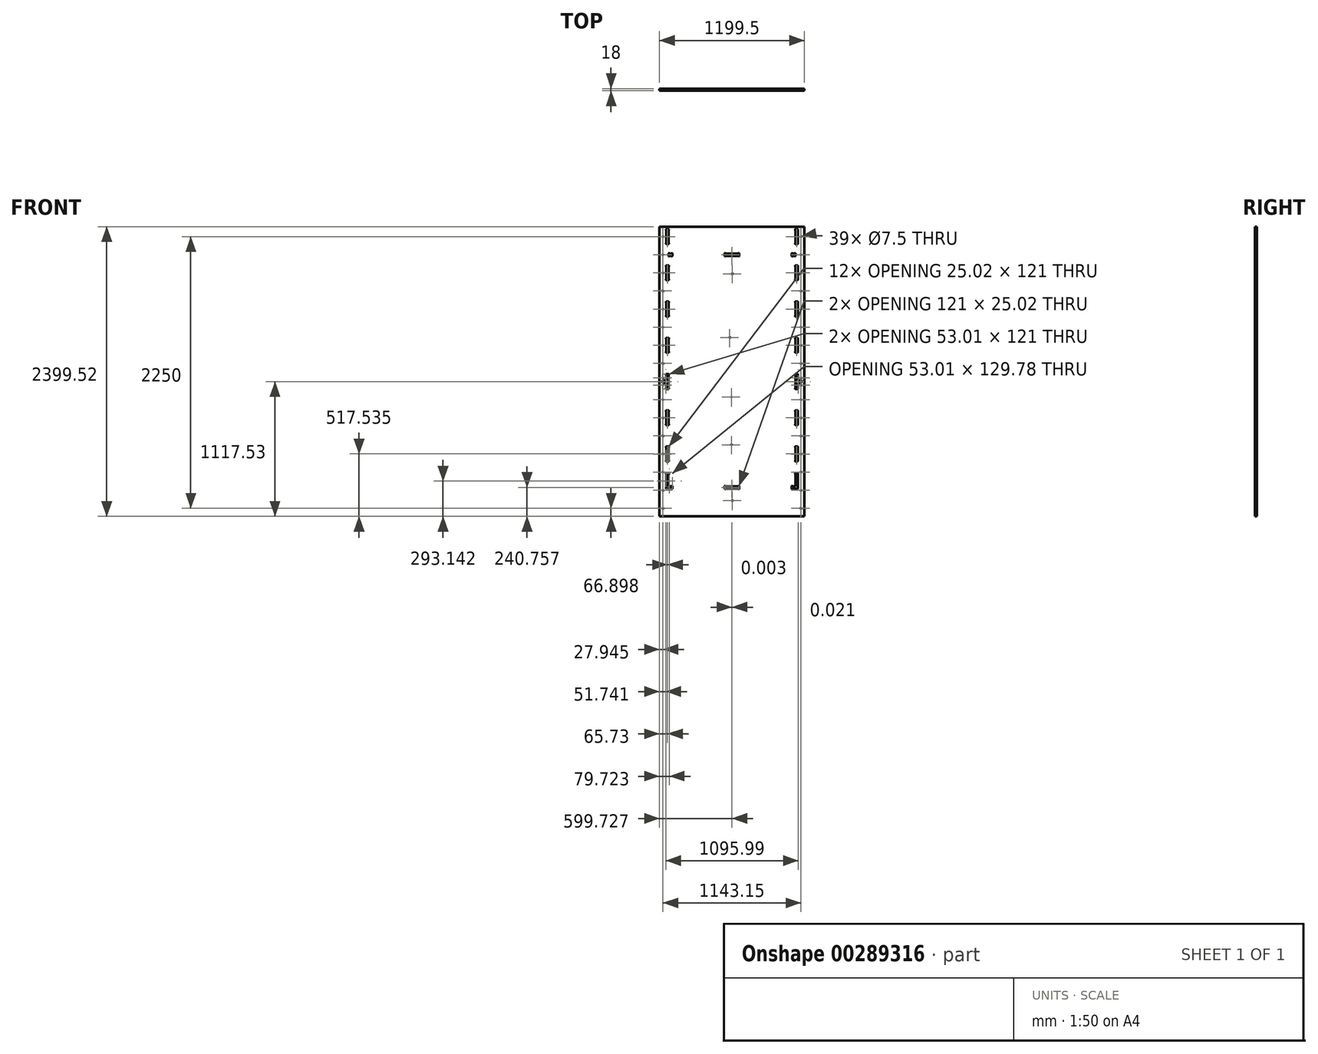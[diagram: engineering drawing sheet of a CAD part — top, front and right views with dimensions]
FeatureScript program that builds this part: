
annotation { "Feature Type Name" : "Feature", "Feature Type Description" : "" }
export const myFeature = defineFeature(function(context is Context, id is Id, definition is map)
    precondition{}
    {
        {
            var Q0;
            Q0=qCreatedBy(makeId("Front.planeOp"),FACE);
            var sketch = newSketch(context, id + "F0", { "sketchPlane" : qUnion([Q0])});
            skLineSegment(sketch, "E0", {"start": v(-600, -1200) * mm, "end": v(600, -1200) * mm});
            skLineSegment(sketch, "E1", {"start": v(600, -1200) * mm, "end": v(600, 1200) * mm});
            skLineSegment(sketch, "E2", {"start": v(600, 1200) * mm, "end": v(-600, 1200) * mm});
            skLineSegment(sketch, "E3", {"start": v(-600, 1200) * mm, "end": v(-600, -1200) * mm});
            skLineSegment(sketch, "E4", {"start": v(599.48, -1200) * mm, "end": v(599.5, 1199.5) * mm});
            skLineSegment(sketch, "E5", {"start": v(599.5, 1199.5) * mm, "end": v(-600, 1199.52) * mm});
            skArc(sketch, "E6", {"start": v(-543.76, -136.46) * mm, "mid": v(-546.77, -139.83) * mm, "end": v(-543.51, -142.97) * mm});
            skLineSegment(sketch, "E7", {"start": v(-543.51, -142.97) * mm, "end": v(-525.01, -142.97) * mm});
            skArc(sketch, "E8", {"start": v(-525.01, -142.97) * mm, "mid": v(-521.76, -139.83) * mm, "end": v(-524.76, -136.46) * mm});
            skLineSegment(sketch, "E9", {"start": v(-524.76, -136.46) * mm, "end": v(-524.76, -28.48) * mm});
            skArc(sketch, "E10", {"start": v(-524.76, -28.48) * mm, "mid": v(-521.76, -25.1) * mm, "end": v(-525.01, -21.97) * mm});
            skLineSegment(sketch, "E11", {"start": v(-525.01, -21.97) * mm, "end": v(-543.51, -21.97) * mm});
            skArc(sketch, "E12", {"start": v(-543.51, -21.97) * mm, "mid": v(-546.77, -25.1) * mm, "end": v(-543.76, -28.48) * mm});
            skLineSegment(sketch, "E13", {"start": v(-543.76, -28.48) * mm, "end": v(-543.76, -72.97) * mm});
            skLineSegment(sketch, "E14", {"start": v(-543.76, -72.97) * mm, "end": v(-568.25, -72.97) * mm});
            skArc(sketch, "E15", {"start": v(-568.25, -72.97) * mm, "mid": v(-571.63, -69.96) * mm, "end": v(-574.76, -73.22) * mm});
            skLineSegment(sketch, "E16", {"start": v(-574.76, -73.22) * mm, "end": v(-574.76, -91.72) * mm});
            skArc(sketch, "E17", {"start": v(-574.76, -91.72) * mm, "mid": v(-571.63, -94.98) * mm, "end": v(-568.25, -91.97) * mm});
            skLineSegment(sketch, "E18", {"start": v(-568.25, -91.97) * mm, "end": v(-543.76, -91.97) * mm});
            skLineSegment(sketch, "E19", {"start": v(-543.76, -91.97) * mm, "end": v(-543.76, -136.46) * mm});
            skArc(sketch, "E20", {"start": v(-525.01, 157.04) * mm, "mid": v(-521.75, 160.17) * mm, "end": v(-524.76, 163.55) * mm});
            skLineSegment(sketch, "E21", {"start": v(-524.76, 163.55) * mm, "end": v(-524.76, 271.52) * mm});
            skArc(sketch, "E22", {"start": v(-524.76, 271.52) * mm, "mid": v(-521.75, 274.9) * mm, "end": v(-525.01, 278.04) * mm});
            skLineSegment(sketch, "E23", {"start": v(-525.01, 278.04) * mm, "end": v(-543.51, 278.04) * mm});
            skArc(sketch, "E24", {"start": v(-543.51, 278.04) * mm, "mid": v(-546.77, 274.9) * mm, "end": v(-543.76, 271.52) * mm});
            skLineSegment(sketch, "E25", {"start": v(-543.76, 271.52) * mm, "end": v(-543.76, 163.55) * mm});
            skArc(sketch, "E26", {"start": v(-543.76, 163.55) * mm, "mid": v(-546.77, 160.17) * mm, "end": v(-543.51, 157.04) * mm});
            skLineSegment(sketch, "E27", {"start": v(-543.51, 157.04) * mm, "end": v(-525.01, 157.04) * mm});
            skArc(sketch, "E28", {"start": v(524.24, 163.53) * mm, "mid": v(521.23, 160.16) * mm, "end": v(524.49, 157.02) * mm});
            skLineSegment(sketch, "E29", {"start": v(524.49, 157.02) * mm, "end": v(542.99, 157.02) * mm});
            skArc(sketch, "E30", {"start": v(542.99, 157.02) * mm, "mid": v(546.25, 160.16) * mm, "end": v(543.24, 163.53) * mm});
            skLineSegment(sketch, "E31", {"start": v(543.24, 163.53) * mm, "end": v(543.24, 271.5) * mm});
            skArc(sketch, "E32", {"start": v(543.24, 271.5) * mm, "mid": v(546.25, 274.89) * mm, "end": v(543, 278.02) * mm});
            skLineSegment(sketch, "E33", {"start": v(543, 278.02) * mm, "end": v(524.5, 278.02) * mm});
            skArc(sketch, "E34", {"start": v(524.5, 278.02) * mm, "mid": v(521.23, 274.89) * mm, "end": v(524.24, 271.5) * mm});
            skLineSegment(sketch, "E35", {"start": v(524.24, 271.5) * mm, "end": v(524.24, 163.53) * mm});
            skArc(sketch, "E36", {"start": v(524.24, 463.53) * mm, "mid": v(521.24, 460.16) * mm, "end": v(524.5, 457.02) * mm});
            skLineSegment(sketch, "E37", {"start": v(524.5, 457.02) * mm, "end": v(543, 457.02) * mm});
            skArc(sketch, "E38", {"start": v(543, 457.02) * mm, "mid": v(546.25, 460.16) * mm, "end": v(543.24, 463.53) * mm});
            skLineSegment(sketch, "E39", {"start": v(543.24, 463.53) * mm, "end": v(543.24, 571.5) * mm});
            skArc(sketch, "E40", {"start": v(543.24, 571.5) * mm, "mid": v(546.25, 574.89) * mm, "end": v(543, 578.02) * mm});
            skLineSegment(sketch, "E41", {"start": v(543, 578.02) * mm, "end": v(524.5, 578.02) * mm});
            skArc(sketch, "E42", {"start": v(524.5, 578.02) * mm, "mid": v(521.24, 574.89) * mm, "end": v(524.24, 571.5) * mm});
            skLineSegment(sketch, "E43", {"start": v(524.24, 571.5) * mm, "end": v(524.24, 463.53) * mm});
            skArc(sketch, "E44", {"start": v(524.25, 763.53) * mm, "mid": v(521.24, 760.16) * mm, "end": v(524.5, 757.02) * mm});
            skLineSegment(sketch, "E45", {"start": v(524.5, 757.02) * mm, "end": v(543, 757.02) * mm});
            skArc(sketch, "E46", {"start": v(543, 757.02) * mm, "mid": v(546.25, 760.16) * mm, "end": v(543.25, 763.53) * mm});
            skLineSegment(sketch, "E47", {"start": v(543.25, 763.53) * mm, "end": v(543.25, 871.51) * mm});
            skArc(sketch, "E48", {"start": v(543.25, 871.51) * mm, "mid": v(546.26, 874.89) * mm, "end": v(543, 878.02) * mm});
            skLineSegment(sketch, "E49", {"start": v(543, 878.02) * mm, "end": v(524.5, 878.02) * mm});
            skArc(sketch, "E50", {"start": v(524.5, 878.02) * mm, "mid": v(521.24, 874.89) * mm, "end": v(524.25, 871.51) * mm});
            skLineSegment(sketch, "E51", {"start": v(524.25, 871.51) * mm, "end": v(524.25, 763.53) * mm});
            skArc(sketch, "E52", {"start": v(518.74, 958.02) * mm, "mid": v(522.11, 955.01) * mm, "end": v(525.25, 958.27) * mm});
            skLineSegment(sketch, "E53", {"start": v(525.25, 958.27) * mm, "end": v(525.25, 976.77) * mm});
            skArc(sketch, "E54", {"start": v(525.25, 976.77) * mm, "mid": v(522.11, 980.03) * mm, "end": v(518.74, 977.02) * mm});
            skLineSegment(sketch, "E55", {"start": v(518.74, 977.02) * mm, "end": v(500.76, 977.02) * mm});
            skArc(sketch, "E56", {"start": v(500.76, 977.02) * mm, "mid": v(497.38, 980.03) * mm, "end": v(494.25, 976.77) * mm});
            skLineSegment(sketch, "E57", {"start": v(494.25, 976.77) * mm, "end": v(494.25, 958.27) * mm});
            skArc(sketch, "E58", {"start": v(494.25, 958.27) * mm, "mid": v(497.38, 955.01) * mm, "end": v(500.76, 958.02) * mm});
            skLineSegment(sketch, "E59", {"start": v(500.76, 958.02) * mm, "end": v(518.74, 958.02) * mm});
            skArc(sketch, "E60", {"start": v(60.25, 976.78) * mm, "mid": v(57.11, 980.04) * mm, "end": v(53.74, 977.03) * mm});
            skLineSegment(sketch, "E61", {"start": v(53.74, 977.03) * mm, "end": v(-54.24, 977.03) * mm});
            skArc(sketch, "E62", {"start": v(-54.24, 977.03) * mm, "mid": v(-57.62, 980.04) * mm, "end": v(-60.75, 976.78) * mm});
            skLineSegment(sketch, "E63", {"start": v(-60.75, 976.78) * mm, "end": v(-60.75, 958.28) * mm});
            skArc(sketch, "E64", {"start": v(-60.75, 958.28) * mm, "mid": v(-57.62, 955.02) * mm, "end": v(-54.24, 958.03) * mm});
            skLineSegment(sketch, "E65", {"start": v(-54.24, 958.03) * mm, "end": v(53.74, 958.03) * mm});
            skArc(sketch, "E66", {"start": v(53.74, 958.03) * mm, "mid": v(57.11, 955.02) * mm, "end": v(60.25, 958.28) * mm});
            skLineSegment(sketch, "E67", {"start": v(60.25, 958.28) * mm, "end": v(60.25, 976.78) * mm});
            skArc(sketch, "E68", {"start": v(-494.75, 976.78) * mm, "mid": v(-497.89, 980.04) * mm, "end": v(-501.26, 977.03) * mm});
            skLineSegment(sketch, "E69", {"start": v(-501.26, 977.03) * mm, "end": v(-519.24, 977.03) * mm});
            skArc(sketch, "E70", {"start": v(-519.24, 977.03) * mm, "mid": v(-522.62, 980.04) * mm, "end": v(-525.75, 976.78) * mm});
            skLineSegment(sketch, "E71", {"start": v(-525.75, 976.78) * mm, "end": v(-525.75, 958.28) * mm});
            skArc(sketch, "E72", {"start": v(-525.75, 958.28) * mm, "mid": v(-522.62, 955.02) * mm, "end": v(-519.24, 958.03) * mm});
            skLineSegment(sketch, "E73", {"start": v(-519.24, 958.03) * mm, "end": v(-501.26, 958.03) * mm});
            skArc(sketch, "E74", {"start": v(-501.26, 958.03) * mm, "mid": v(-497.89, 955.02) * mm, "end": v(-494.75, 958.28) * mm});
            skLineSegment(sketch, "E75", {"start": v(-494.75, 958.28) * mm, "end": v(-494.75, 976.78) * mm});
            skArc(sketch, "E76", {"start": v(-543.5, 878.04) * mm, "mid": v(-546.76, 874.9) * mm, "end": v(-543.75, 871.53) * mm});
            skLineSegment(sketch, "E77", {"start": v(-543.75, 871.53) * mm, "end": v(-543.75, 763.55) * mm});
            skArc(sketch, "E78", {"start": v(-543.75, 763.55) * mm, "mid": v(-546.76, 760.17) * mm, "end": v(-543.5, 757.04) * mm});
            skLineSegment(sketch, "E79", {"start": v(-543.5, 757.04) * mm, "end": v(-525, 757.04) * mm});
            skArc(sketch, "E80", {"start": v(-525, 757.04) * mm, "mid": v(-521.75, 760.17) * mm, "end": v(-524.75, 763.55) * mm});
            skLineSegment(sketch, "E81", {"start": v(-524.75, 763.55) * mm, "end": v(-524.75, 871.53) * mm});
            skArc(sketch, "E82", {"start": v(-524.75, 871.53) * mm, "mid": v(-521.75, 874.9) * mm, "end": v(-525, 878.04) * mm});
            skLineSegment(sketch, "E83", {"start": v(-525, 878.04) * mm, "end": v(-543.5, 878.04) * mm});
            skArc(sketch, "E84", {"start": v(-524.76, 571.52) * mm, "mid": v(-521.75, 574.9) * mm, "end": v(-525, 578.04) * mm});
            skLineSegment(sketch, "E85", {"start": v(-525, 578.04) * mm, "end": v(-543.5, 578.04) * mm});
            skArc(sketch, "E86", {"start": v(-543.5, 578.04) * mm, "mid": v(-546.77, 574.9) * mm, "end": v(-543.76, 571.53) * mm});
            skLineSegment(sketch, "E87", {"start": v(-543.76, 571.53) * mm, "end": v(-543.76, 463.55) * mm});
            skArc(sketch, "E88", {"start": v(-543.76, 463.55) * mm, "mid": v(-546.77, 460.17) * mm, "end": v(-543.5, 457.04) * mm});
            skLineSegment(sketch, "E89", {"start": v(-543.5, 457.04) * mm, "end": v(-525, 457.04) * mm});
            skArc(sketch, "E90", {"start": v(-525, 457.04) * mm, "mid": v(-521.75, 460.17) * mm, "end": v(-524.76, 463.55) * mm});
            skLineSegment(sketch, "E91", {"start": v(-524.76, 463.55) * mm, "end": v(-524.76, 571.52) * mm});
            skArc(sketch, "E92", {"start": v(-525, 1057.04) * mm, "mid": v(-521.74, 1060.17) * mm, "end": v(-524.75, 1063.55) * mm});
            skLineSegment(sketch, "E93", {"start": v(-524.75, 1063.55) * mm, "end": v(-524.75, 1171.53) * mm});
            skArc(sketch, "E94", {"start": v(-524.75, 1171.53) * mm, "mid": v(-521.74, 1174.9) * mm, "end": v(-525, 1178.04) * mm});
            skLineSegment(sketch, "E95", {"start": v(-525, 1178.04) * mm, "end": v(-543.5, 1178.04) * mm});
            skArc(sketch, "E96", {"start": v(-543.5, 1178.04) * mm, "mid": v(-546.76, 1174.9) * mm, "end": v(-543.75, 1171.53) * mm});
            skLineSegment(sketch, "E97", {"start": v(-543.75, 1171.53) * mm, "end": v(-543.75, 1063.55) * mm});
            skArc(sketch, "E98", {"start": v(-543.75, 1063.55) * mm, "mid": v(-546.76, 1060.17) * mm, "end": v(-543.5, 1057.04) * mm});
            skLineSegment(sketch, "E99", {"start": v(-543.5, 1057.04) * mm, "end": v(-525, 1057.04) * mm});
            skArc(sketch, "E100", {"start": v(543, 1057.02) * mm, "mid": v(546.26, 1060.16) * mm, "end": v(543.25, 1063.53) * mm});
            skLineSegment(sketch, "E101", {"start": v(543.25, 1063.53) * mm, "end": v(543.25, 1171.51) * mm});
            skArc(sketch, "E102", {"start": v(543.25, 1171.51) * mm, "mid": v(546.26, 1174.89) * mm, "end": v(543, 1178.02) * mm});
            skLineSegment(sketch, "E103", {"start": v(543, 1178.02) * mm, "end": v(524.5, 1178.02) * mm});
            skArc(sketch, "E104", {"start": v(524.5, 1178.02) * mm, "mid": v(521.24, 1174.89) * mm, "end": v(524.25, 1171.51) * mm});
            skLineSegment(sketch, "E105", {"start": v(524.25, 1171.51) * mm, "end": v(524.25, 1063.53) * mm});
            skArc(sketch, "E106", {"start": v(524.25, 1063.53) * mm, "mid": v(521.24, 1060.16) * mm, "end": v(524.5, 1057.02) * mm});
            skLineSegment(sketch, "E107", {"start": v(524.5, 1057.02) * mm, "end": v(543, 1057.02) * mm});
            skArc(sketch, "E108", {"start": v(524.49, -21.98) * mm, "mid": v(521.23, -25.11) * mm, "end": v(524.24, -28.5) * mm});
            skLineSegment(sketch, "E109", {"start": v(524.24, -28.5) * mm, "end": v(524.24, -136.47) * mm});
            skArc(sketch, "E110", {"start": v(524.24, -136.47) * mm, "mid": v(521.23, -139.84) * mm, "end": v(524.49, -142.98) * mm});
            skLineSegment(sketch, "E111", {"start": v(524.49, -142.98) * mm, "end": v(542.99, -142.98) * mm});
            skArc(sketch, "E112", {"start": v(542.99, -142.98) * mm, "mid": v(546.25, -139.84) * mm, "end": v(543.24, -136.47) * mm});
            skLineSegment(sketch, "E113", {"start": v(543.24, -136.47) * mm, "end": v(543.24, -91.98) * mm});
            skLineSegment(sketch, "E114", {"start": v(543.24, -91.98) * mm, "end": v(567.73, -91.98) * mm});
            skArc(sketch, "E115", {"start": v(567.73, -91.98) * mm, "mid": v(571.1, -95) * mm, "end": v(574.24, -91.73) * mm});
            skLineSegment(sketch, "E116", {"start": v(574.24, -91.73) * mm, "end": v(574.24, -73.23) * mm});
            skArc(sketch, "E117", {"start": v(574.24, -73.23) * mm, "mid": v(571.1, -69.98) * mm, "end": v(567.73, -72.98) * mm});
            skLineSegment(sketch, "E118", {"start": v(567.73, -72.98) * mm, "end": v(543.24, -72.98) * mm});
            skLineSegment(sketch, "E119", {"start": v(543.24, -72.98) * mm, "end": v(543.24, -28.5) * mm});
            skArc(sketch, "E120", {"start": v(543.24, -28.5) * mm, "mid": v(546.25, -25.11) * mm, "end": v(542.99, -21.98) * mm});
            skLineSegment(sketch, "E121", {"start": v(542.99, -21.98) * mm, "end": v(524.49, -21.98) * mm});
            skArc(sketch, "E122", {"start": v(-524.77, -328.48) * mm, "mid": v(-521.76, -325.1) * mm, "end": v(-525.02, -321.96) * mm});
            skLineSegment(sketch, "E123", {"start": v(-525.02, -321.96) * mm, "end": v(-543.52, -321.96) * mm});
            skArc(sketch, "E124", {"start": v(-543.52, -321.96) * mm, "mid": v(-546.78, -325.1) * mm, "end": v(-543.77, -328.48) * mm});
            skLineSegment(sketch, "E125", {"start": v(-543.77, -328.48) * mm, "end": v(-543.77, -436.45) * mm});
            skArc(sketch, "E126", {"start": v(-543.77, -436.45) * mm, "mid": v(-546.78, -439.83) * mm, "end": v(-543.52, -442.96) * mm});
            skLineSegment(sketch, "E127", {"start": v(-543.52, -442.96) * mm, "end": v(-525.02, -442.96) * mm});
            skArc(sketch, "E128", {"start": v(-525.02, -442.96) * mm, "mid": v(-521.76, -439.83) * mm, "end": v(-524.77, -436.45) * mm});
            skLineSegment(sketch, "E129", {"start": v(-524.77, -436.45) * mm, "end": v(-524.77, -328.48) * mm});
            skArc(sketch, "E130", {"start": v(-524.77, -628.48) * mm, "mid": v(-521.76, -625.1) * mm, "end": v(-525.02, -621.96) * mm});
            skLineSegment(sketch, "E131", {"start": v(-525.02, -621.96) * mm, "end": v(-543.52, -621.96) * mm});
            skArc(sketch, "E132", {"start": v(-543.52, -621.96) * mm, "mid": v(-546.78, -625.1) * mm, "end": v(-543.77, -628.48) * mm});
            skLineSegment(sketch, "E133", {"start": v(-543.77, -628.48) * mm, "end": v(-543.77, -736.45) * mm});
            skArc(sketch, "E134", {"start": v(-543.77, -736.45) * mm, "mid": v(-546.78, -739.83) * mm, "end": v(-543.52, -742.96) * mm});
            skLineSegment(sketch, "E135", {"start": v(-543.52, -742.96) * mm, "end": v(-525.02, -742.97) * mm});
            skArc(sketch, "E136", {"start": v(-525.02, -742.97) * mm, "mid": v(-521.76, -739.83) * mm, "end": v(-524.77, -736.45) * mm});
            skLineSegment(sketch, "E137", {"start": v(-524.77, -736.45) * mm, "end": v(-524.77, -628.48) * mm});
            skArc(sketch, "E138", {"start": v(-54.26, -949.74) * mm, "mid": v(-57.64, -946.73) * mm, "end": v(-60.77, -950) * mm});
            skLineSegment(sketch, "E139", {"start": v(-60.77, -950) * mm, "end": v(-60.77, -968.5) * mm});
            skArc(sketch, "E140", {"start": v(-60.77, -968.5) * mm, "mid": v(-57.64, -971.75) * mm, "end": v(-54.26, -968.74) * mm});
            skLineSegment(sketch, "E141", {"start": v(-54.26, -968.74) * mm, "end": v(53.72, -968.74) * mm});
            skArc(sketch, "E142", {"start": v(53.72, -968.74) * mm, "mid": v(57.1, -971.75) * mm, "end": v(60.23, -968.5) * mm});
            skLineSegment(sketch, "E143", {"start": v(60.23, -968.5) * mm, "end": v(60.23, -950) * mm});
            skArc(sketch, "E144", {"start": v(60.23, -950) * mm, "mid": v(57.1, -946.74) * mm, "end": v(53.72, -949.74) * mm});
            skLineSegment(sketch, "E145", {"start": v(53.72, -949.74) * mm, "end": v(-54.26, -949.74) * mm});
            skLineSegment(sketch, "E146", {"start": v(524.23, -628.5) * mm, "end": v(524.23, -736.47) * mm});
            skArc(sketch, "E147", {"start": v(524.23, -736.47) * mm, "mid": v(521.22, -739.84) * mm, "end": v(524.48, -742.98) * mm});
            skLineSegment(sketch, "E148", {"start": v(524.48, -742.98) * mm, "end": v(542.98, -742.98) * mm});
            skArc(sketch, "E149", {"start": v(542.98, -742.98) * mm, "mid": v(546.24, -739.84) * mm, "end": v(543.23, -736.47) * mm});
            skLineSegment(sketch, "E150", {"start": v(543.23, -736.47) * mm, "end": v(543.23, -628.5) * mm});
            skArc(sketch, "E151", {"start": v(543.23, -628.5) * mm, "mid": v(546.24, -625.12) * mm, "end": v(542.98, -621.98) * mm});
            skLineSegment(sketch, "E152", {"start": v(542.98, -621.98) * mm, "end": v(524.48, -621.98) * mm});
            skArc(sketch, "E153", {"start": v(524.48, -621.98) * mm, "mid": v(521.22, -625.12) * mm, "end": v(524.23, -628.5) * mm});
            skArc(sketch, "E154", {"start": v(524.23, -436.47) * mm, "mid": v(521.23, -439.84) * mm, "end": v(524.48, -442.98) * mm});
            skLineSegment(sketch, "E155", {"start": v(524.48, -442.98) * mm, "end": v(542.98, -442.98) * mm});
            skArc(sketch, "E156", {"start": v(542.98, -442.98) * mm, "mid": v(546.24, -439.84) * mm, "end": v(543.23, -436.47) * mm});
            skLineSegment(sketch, "E157", {"start": v(543.23, -436.47) * mm, "end": v(543.23, -328.5) * mm});
            skArc(sketch, "E158", {"start": v(543.23, -328.5) * mm, "mid": v(546.24, -325.12) * mm, "end": v(542.98, -321.98) * mm});
            skLineSegment(sketch, "E159", {"start": v(542.98, -321.98) * mm, "end": v(524.48, -321.98) * mm});
            skArc(sketch, "E160", {"start": v(524.48, -321.98) * mm, "mid": v(521.23, -325.11) * mm, "end": v(524.23, -328.5) * mm});
            skLineSegment(sketch, "E161", {"start": v(524.23, -328.5) * mm, "end": v(524.23, -436.47) * mm});
            skArc(sketch, "E162", {"start": v(524.48, -841.98) * mm, "mid": v(521.22, -845.12) * mm, "end": v(524.23, -848.5) * mm});
            skLineSegment(sketch, "E163", {"start": v(524.23, -848.5) * mm, "end": v(524.23, -949.75) * mm});
            skLineSegment(sketch, "E164", {"start": v(524.23, -949.75) * mm, "end": v(499.74, -949.75) * mm});
            skArc(sketch, "E165", {"start": v(499.74, -949.75) * mm, "mid": v(496.36, -946.74) * mm, "end": v(493.23, -950) * mm});
            skLineSegment(sketch, "E166", {"start": v(493.23, -950) * mm, "end": v(493.23, -968.5) * mm});
            skArc(sketch, "E167", {"start": v(493.23, -968.5) * mm, "mid": v(496.36, -971.76) * mm, "end": v(499.74, -968.75) * mm});
            skLineSegment(sketch, "E168", {"start": v(499.74, -968.75) * mm, "end": v(542.98, -968.75) * mm});
            skArc(sketch, "E169", {"start": v(542.98, -968.75) * mm, "mid": v(546.24, -965.61) * mm, "end": v(543.23, -962.24) * mm});
            skLineSegment(sketch, "E170", {"start": v(543.23, -962.24) * mm, "end": v(543.23, -848.5) * mm});
            skArc(sketch, "E171", {"start": v(543.23, -848.5) * mm, "mid": v(546.24, -845.12) * mm, "end": v(542.98, -841.98) * mm});
            skLineSegment(sketch, "E172", {"start": v(542.98, -841.98) * mm, "end": v(524.48, -841.98) * mm});
            skArc(sketch, "E173", {"start": v(-543.52, -841.97) * mm, "mid": v(-546.78, -845.1) * mm, "end": v(-543.77, -848.48) * mm});
            skLineSegment(sketch, "E174", {"start": v(-543.77, -848.48) * mm, "end": v(-543.77, -962.23) * mm});
            skArc(sketch, "E175", {"start": v(-543.77, -962.23) * mm, "mid": v(-546.78, -965.6) * mm, "end": v(-543.52, -968.74) * mm});
            skLineSegment(sketch, "E176", {"start": v(-543.52, -968.74) * mm, "end": v(-500.28, -968.74) * mm});
            skArc(sketch, "E177", {"start": v(-500.28, -968.74) * mm, "mid": v(-496.9, -971.75) * mm, "end": v(-493.77, -968.49) * mm});
            skLineSegment(sketch, "E178", {"start": v(-493.77, -968.49) * mm, "end": v(-493.77, -949.99) * mm});
            skArc(sketch, "E179", {"start": v(-493.77, -949.99) * mm, "mid": v(-496.9, -946.73) * mm, "end": v(-500.28, -949.74) * mm});
            skLineSegment(sketch, "E180", {"start": v(-500.28, -949.74) * mm, "end": v(-524.77, -949.74) * mm});
            skLineSegment(sketch, "E181", {"start": v(-524.77, -949.74) * mm, "end": v(-524.77, -848.48) * mm});
            skArc(sketch, "E182", {"start": v(-524.77, -848.48) * mm, "mid": v(-521.76, -845.1) * mm, "end": v(-525.02, -841.97) * mm});
            skLineSegment(sketch, "E183", {"start": v(-525.02, -841.97) * mm, "end": v(-543.52, -841.97) * mm});
            skLineSegment(sketch, "E184", {"start": v(-134.09, -74.33) * mm, "end": v(-123.64, -114.32) * mm});
            skLineSegment(sketch, "E185", {"start": v(-123.64, -114.32) * mm, "end": v(-122.54, -114.32) * mm});
            skLineSegment(sketch, "E186", {"start": v(-122.54, -114.32) * mm, "end": v(-111.31, -74.33) * mm});
            skLineSegment(sketch, "E187", {"start": v(-111.31, -74.33) * mm, "end": v(-109.95, -74.33) * mm});
            skLineSegment(sketch, "E188", {"start": v(-109.95, -74.33) * mm, "end": v(-98, -114.32) * mm});
            skLineSegment(sketch, "E189", {"start": v(-98, -114.32) * mm, "end": v(-96.62, -114.32) * mm});
            skLineSegment(sketch, "E190", {"start": v(-96.62, -114.32) * mm, "end": v(-86.93, -74.33) * mm});
            skLineSegment(sketch, "E191", {"start": v(-87.47, -114.31) * mm, "end": v(-73.16, -74.31) * mm});
            skLineSegment(sketch, "E192", {"start": v(-73.16, -74.31) * mm, "end": v(-71, -74.31) * mm});
            skLineSegment(sketch, "E193", {"start": v(-71, -74.31) * mm, "end": v(-55.72, -114.31) * mm});
            skLineSegment(sketch, "E194", {"start": v(-82.44, -100.32) * mm, "end": v(-61.18, -100.32) * mm});
            skLineSegment(sketch, "E195", {"start": v(-23.2, -114.3) * mm, "end": v(-46.7, -114.3) * mm});
            skLineSegment(sketch, "E196", {"start": v(-46.7, -114.3) * mm, "end": v(-46.7, -74.35) * mm});
            skLineSegment(sketch, "E197", {"start": v(9.1, -114.3) * mm, "end": v(-14.4, -114.3) * mm});
            skLineSegment(sketch, "E198", {"start": v(-14.4, -114.3) * mm, "end": v(-14.4, -74.35) * mm});
            skLineSegment(sketch, "E199", {"start": v(44.22, -81.02) * mm, "end": v(44.8, -81.02) * mm});
            skLineSegment(sketch, "E200", {"start": v(44.8, -81.02) * mm, "end": v(45.4, -81) * mm});
            skLineSegment(sketch, "E201", {"start": v(45.4, -81) * mm, "end": v(45.97, -80.95) * mm});
            skLineSegment(sketch, "E202", {"start": v(45.97, -80.95) * mm, "end": v(46.53, -80.89) * mm});
            skLineSegment(sketch, "E203", {"start": v(46.53, -80.89) * mm, "end": v(47.09, -80.81) * mm});
            skLineSegment(sketch, "E204", {"start": v(47.09, -80.81) * mm, "end": v(47.63, -80.72) * mm});
            skLineSegment(sketch, "E205", {"start": v(47.63, -80.72) * mm, "end": v(48.17, -80.62) * mm});
            skLineSegment(sketch, "E206", {"start": v(48.17, -80.62) * mm, "end": v(48.69, -80.5) * mm});
            skLineSegment(sketch, "E207", {"start": v(48.69, -80.5) * mm, "end": v(49.2, -80.36) * mm});
            skLineSegment(sketch, "E208", {"start": v(49.2, -80.36) * mm, "end": v(49.7, -80.21) * mm});
            skLineSegment(sketch, "E209", {"start": v(49.7, -80.21) * mm, "end": v(50.17, -80.05) * mm});
            skLineSegment(sketch, "E210", {"start": v(50.17, -80.05) * mm, "end": v(50.64, -79.88) * mm});
            skLineSegment(sketch, "E211", {"start": v(50.64, -79.88) * mm, "end": v(51.1, -79.69) * mm});
            skLineSegment(sketch, "E212", {"start": v(51.1, -79.69) * mm, "end": v(51.53, -79.5) * mm});
            skLineSegment(sketch, "E213", {"start": v(51.53, -79.5) * mm, "end": v(51.94, -79.28) * mm});
            skLineSegment(sketch, "E214", {"start": v(51.94, -79.28) * mm, "end": v(52.34, -79.06) * mm});
            skLineSegment(sketch, "E215", {"start": v(52.34, -79.06) * mm, "end": v(52.72, -78.82) * mm});
            skLineSegment(sketch, "E216", {"start": v(52.72, -78.82) * mm, "end": v(53.08, -78.58) * mm});
            skLineSegment(sketch, "E217", {"start": v(53.08, -78.58) * mm, "end": v(53.43, -78.33) * mm});
            skLineSegment(sketch, "E218", {"start": v(53.43, -78.33) * mm, "end": v(53.75, -78.06) * mm});
            skLineSegment(sketch, "E219", {"start": v(53.75, -78.06) * mm, "end": v(54.04, -77.79) * mm});
            skLineSegment(sketch, "E220", {"start": v(54.04, -77.79) * mm, "end": v(54.32, -77.5) * mm});
            skLineSegment(sketch, "E221", {"start": v(54.32, -77.5) * mm, "end": v(54.58, -77.22) * mm});
            skLineSegment(sketch, "E222", {"start": v(54.58, -77.22) * mm, "end": v(54.8, -76.92) * mm});
            skLineSegment(sketch, "E223", {"start": v(54.8, -76.92) * mm, "end": v(55.01, -76.62) * mm});
            skLineSegment(sketch, "E224", {"start": v(55.01, -76.62) * mm, "end": v(55.2, -76.3) * mm});
            skLineSegment(sketch, "E225", {"start": v(55.2, -76.3) * mm, "end": v(55.35, -75.98) * mm});
            skLineSegment(sketch, "E226", {"start": v(55.35, -75.98) * mm, "end": v(55.48, -75.66) * mm});
            skLineSegment(sketch, "E227", {"start": v(55.48, -75.66) * mm, "end": v(55.58, -75.33) * mm});
            skLineSegment(sketch, "E228", {"start": v(55.58, -75.33) * mm, "end": v(55.65, -75) * mm});
            skLineSegment(sketch, "E229", {"start": v(55.65, -75) * mm, "end": v(55.7, -74.65) * mm});
            skLineSegment(sketch, "E230", {"start": v(55.7, -74.65) * mm, "end": v(55.7, -74.48) * mm});
            skLineSegment(sketch, "E231", {"start": v(55.7, -74.48) * mm, "end": v(55.7, -74.3) * mm});
            skLineSegment(sketch, "E232", {"start": v(55.7, -74.3) * mm, "end": v(56.35, -74.3) * mm});
            skLineSegment(sketch, "E233", {"start": v(56.35, -74.3) * mm, "end": v(56.35, -114.3) * mm});
            skArc(sketch, "E234", {"start": v(-575.8, 1116.9) * mm, "mid": v(-574.7, 1119.55) * mm, "end": v(-572.05, 1120.65) * mm});
            skArc(sketch, "E235", {"start": v(-572.05, 1120.65) * mm, "mid": v(-569.4, 1119.55) * mm, "end": v(-568.3, 1116.9) * mm});
            skArc(sketch, "E236", {"start": v(-568.3, 1116.9) * mm, "mid": v(-569.4, 1114.25) * mm, "end": v(-572.05, 1113.15) * mm});
            skArc(sketch, "E237", {"start": v(-572.05, 1113.15) * mm, "mid": v(-574.7, 1114.25) * mm, "end": v(-575.8, 1116.9) * mm});
            skArc(sketch, "E238", {"start": v(-575.8, 966.9) * mm, "mid": v(-574.7, 969.55) * mm, "end": v(-572.05, 970.65) * mm});
            skArc(sketch, "E239", {"start": v(-572.05, 970.65) * mm, "mid": v(-569.4, 969.55) * mm, "end": v(-568.3, 966.9) * mm});
            skArc(sketch, "E240", {"start": v(-568.3, 966.9) * mm, "mid": v(-569.4, 964.25) * mm, "end": v(-572.05, 963.15) * mm});
            skArc(sketch, "E241", {"start": v(-572.05, 963.15) * mm, "mid": v(-574.7, 964.25) * mm, "end": v(-575.8, 966.9) * mm});
            skArc(sketch, "E242", {"start": v(-575.8, 816.9) * mm, "mid": v(-574.7, 819.55) * mm, "end": v(-572.05, 820.65) * mm});
            skArc(sketch, "E243", {"start": v(-572.05, 820.65) * mm, "mid": v(-569.4, 819.55) * mm, "end": v(-568.3, 816.9) * mm});
            skArc(sketch, "E244", {"start": v(-568.3, 816.9) * mm, "mid": v(-569.4, 814.25) * mm, "end": v(-572.05, 813.15) * mm});
            skArc(sketch, "E245", {"start": v(-572.05, 813.15) * mm, "mid": v(-574.7, 814.25) * mm, "end": v(-575.8, 816.9) * mm});
            skArc(sketch, "E246", {"start": v(-575.8, 666.9) * mm, "mid": v(-574.7, 669.55) * mm, "end": v(-572.05, 670.65) * mm});
            skArc(sketch, "E247", {"start": v(-572.05, 670.65) * mm, "mid": v(-569.4, 669.55) * mm, "end": v(-568.3, 666.9) * mm});
            skArc(sketch, "E248", {"start": v(-568.3, 666.9) * mm, "mid": v(-569.4, 664.25) * mm, "end": v(-572.05, 663.15) * mm});
            skArc(sketch, "E249", {"start": v(-572.05, 663.15) * mm, "mid": v(-574.7, 664.25) * mm, "end": v(-575.8, 666.9) * mm});
            skArc(sketch, "E250", {"start": v(-575.8, 516.9) * mm, "mid": v(-574.7, 519.55) * mm, "end": v(-572.05, 520.65) * mm});
            skArc(sketch, "E251", {"start": v(-572.05, 520.65) * mm, "mid": v(-569.4, 519.55) * mm, "end": v(-568.3, 516.9) * mm});
            skArc(sketch, "E252", {"start": v(-568.3, 516.9) * mm, "mid": v(-569.4, 514.25) * mm, "end": v(-572.05, 513.15) * mm});
            skArc(sketch, "E253", {"start": v(-572.05, 513.15) * mm, "mid": v(-574.7, 514.25) * mm, "end": v(-575.8, 516.9) * mm});
            skArc(sketch, "E254", {"start": v(-575.8, 366.9) * mm, "mid": v(-574.7, 369.55) * mm, "end": v(-572.05, 370.65) * mm});
            skArc(sketch, "E255", {"start": v(-572.05, 370.65) * mm, "mid": v(-569.4, 369.55) * mm, "end": v(-568.3, 366.9) * mm});
            skArc(sketch, "E256", {"start": v(-568.3, 366.9) * mm, "mid": v(-569.4, 364.25) * mm, "end": v(-572.05, 363.15) * mm});
            skArc(sketch, "E257", {"start": v(-572.05, 363.15) * mm, "mid": v(-574.7, 364.25) * mm, "end": v(-575.8, 366.9) * mm});
            skArc(sketch, "E258", {"start": v(-575.8, 216.9) * mm, "mid": v(-574.7, 219.55) * mm, "end": v(-572.05, 220.65) * mm});
            skArc(sketch, "E259", {"start": v(-572.05, 220.65) * mm, "mid": v(-569.4, 219.55) * mm, "end": v(-568.3, 216.9) * mm});
            skArc(sketch, "E260", {"start": v(-568.3, 216.9) * mm, "mid": v(-569.4, 214.25) * mm, "end": v(-572.05, 213.15) * mm});
            skArc(sketch, "E261", {"start": v(-572.05, 213.15) * mm, "mid": v(-574.7, 214.25) * mm, "end": v(-575.8, 216.9) * mm});
            skArc(sketch, "E262", {"start": v(-575.8, 66.9) * mm, "mid": v(-574.7, 69.55) * mm, "end": v(-572.05, 70.65) * mm});
            skArc(sketch, "E263", {"start": v(-572.05, 70.65) * mm, "mid": v(-569.4, 69.55) * mm, "end": v(-568.3, 66.9) * mm});
            skArc(sketch, "E264", {"start": v(-568.3, 66.9) * mm, "mid": v(-569.4, 64.25) * mm, "end": v(-572.05, 63.15) * mm});
            skArc(sketch, "E265", {"start": v(-572.05, 63.15) * mm, "mid": v(-574.7, 64.25) * mm, "end": v(-575.8, 66.9) * mm});
            skArc(sketch, "E266", {"start": v(-575.8, -53.1) * mm, "mid": v(-574.7, -50.45) * mm, "end": v(-572.05, -49.35) * mm});
            skArc(sketch, "E267", {"start": v(-572.05, -49.35) * mm, "mid": v(-569.4, -50.45) * mm, "end": v(-568.3, -53.1) * mm});
            skArc(sketch, "E268", {"start": v(-568.3, -53.1) * mm, "mid": v(-569.4, -55.75) * mm, "end": v(-572.05, -56.85) * mm});
            skArc(sketch, "E269", {"start": v(-572.05, -56.85) * mm, "mid": v(-574.7, -55.75) * mm, "end": v(-575.8, -53.1) * mm});
            skArc(sketch, "E270", {"start": v(-575.8, -233.1) * mm, "mid": v(-574.7, -230.45) * mm, "end": v(-572.05, -229.35) * mm});
            skArc(sketch, "E271", {"start": v(-572.05, -229.35) * mm, "mid": v(-569.4, -230.45) * mm, "end": v(-568.3, -233.1) * mm});
            skArc(sketch, "E272", {"start": v(-568.3, -233.1) * mm, "mid": v(-569.4, -235.75) * mm, "end": v(-572.05, -236.85) * mm});
            skArc(sketch, "E273", {"start": v(-572.05, -236.85) * mm, "mid": v(-574.7, -235.75) * mm, "end": v(-575.8, -233.1) * mm});
            skArc(sketch, "E274", {"start": v(-575.8, -383.1) * mm, "mid": v(-574.7, -380.45) * mm, "end": v(-572.05, -379.35) * mm});
            skArc(sketch, "E275", {"start": v(-572.05, -379.35) * mm, "mid": v(-569.4, -380.45) * mm, "end": v(-568.3, -383.1) * mm});
            skArc(sketch, "E276", {"start": v(-568.3, -383.1) * mm, "mid": v(-569.4, -385.75) * mm, "end": v(-572.05, -386.85) * mm});
            skArc(sketch, "E277", {"start": v(-572.05, -386.85) * mm, "mid": v(-574.7, -385.75) * mm, "end": v(-575.8, -383.1) * mm});
            skArc(sketch, "E278", {"start": v(-575.8, -533.1) * mm, "mid": v(-574.7, -530.45) * mm, "end": v(-572.05, -529.35) * mm});
            skArc(sketch, "E279", {"start": v(-572.05, -529.35) * mm, "mid": v(-569.4, -530.45) * mm, "end": v(-568.3, -533.1) * mm});
            skArc(sketch, "E280", {"start": v(-568.3, -533.1) * mm, "mid": v(-569.4, -535.75) * mm, "end": v(-572.05, -536.85) * mm});
            skArc(sketch, "E281", {"start": v(-572.05, -536.85) * mm, "mid": v(-574.7, -535.75) * mm, "end": v(-575.8, -533.1) * mm});
            skArc(sketch, "E282", {"start": v(-575.8, -683.1) * mm, "mid": v(-574.7, -680.45) * mm, "end": v(-572.05, -679.35) * mm});
            skArc(sketch, "E283", {"start": v(-572.05, -679.35) * mm, "mid": v(-569.4, -680.45) * mm, "end": v(-568.3, -683.1) * mm});
            skArc(sketch, "E284", {"start": v(-568.3, -683.1) * mm, "mid": v(-569.4, -685.75) * mm, "end": v(-572.05, -686.85) * mm});
            skArc(sketch, "E285", {"start": v(-572.05, -686.85) * mm, "mid": v(-574.7, -685.75) * mm, "end": v(-575.8, -683.1) * mm});
            skArc(sketch, "E286", {"start": v(-575.8, -833.1) * mm, "mid": v(-574.7, -830.45) * mm, "end": v(-572.05, -829.35) * mm});
            skArc(sketch, "E287", {"start": v(-572.05, -829.35) * mm, "mid": v(-569.4, -830.45) * mm, "end": v(-568.3, -833.1) * mm});
            skArc(sketch, "E288", {"start": v(-568.3, -833.1) * mm, "mid": v(-569.4, -835.75) * mm, "end": v(-572.05, -836.85) * mm});
            skArc(sketch, "E289", {"start": v(-572.05, -836.85) * mm, "mid": v(-574.7, -835.75) * mm, "end": v(-575.8, -833.1) * mm});
            skArc(sketch, "E290", {"start": v(-575.8, -983.1) * mm, "mid": v(-574.7, -980.45) * mm, "end": v(-572.05, -979.35) * mm});
            skArc(sketch, "E291", {"start": v(-572.05, -979.35) * mm, "mid": v(-569.4, -980.45) * mm, "end": v(-568.3, -983.1) * mm});
            skArc(sketch, "E292", {"start": v(-568.3, -983.1) * mm, "mid": v(-569.4, -985.75) * mm, "end": v(-572.05, -986.85) * mm});
            skArc(sketch, "E293", {"start": v(-572.05, -986.85) * mm, "mid": v(-574.7, -985.75) * mm, "end": v(-575.8, -983.1) * mm});
            skArc(sketch, "E294", {"start": v(-575.8, -1133.1) * mm, "mid": v(-574.7, -1130.45) * mm, "end": v(-572.05, -1129.35) * mm});
            skArc(sketch, "E295", {"start": v(-572.05, -1129.35) * mm, "mid": v(-569.4, -1130.45) * mm, "end": v(-568.3, -1133.1) * mm});
            skArc(sketch, "E296", {"start": v(-568.3, -1133.1) * mm, "mid": v(-569.4, -1135.75) * mm, "end": v(-572.05, -1136.85) * mm});
            skArc(sketch, "E297", {"start": v(-572.05, -1136.85) * mm, "mid": v(-574.7, -1135.75) * mm, "end": v(-575.8, -1133.1) * mm});
            skArc(sketch, "E298", {"start": v(-575.8, -113.1) * mm, "mid": v(-574.7, -110.45) * mm, "end": v(-572.05, -109.35) * mm});
            skArc(sketch, "E299", {"start": v(-572.05, -109.35) * mm, "mid": v(-569.4, -110.45) * mm, "end": v(-568.3, -113.1) * mm});
            skArc(sketch, "E300", {"start": v(-568.3, -113.1) * mm, "mid": v(-569.4, -115.75) * mm, "end": v(-572.05, -116.85) * mm});
            skArc(sketch, "E301", {"start": v(-572.05, -116.85) * mm, "mid": v(-574.7, -115.75) * mm, "end": v(-575.8, -113.1) * mm});
            skArc(sketch, "E302", {"start": v(567.35, 1116.9) * mm, "mid": v(568.44, 1119.55) * mm, "end": v(571.1, 1120.65) * mm});
            skArc(sketch, "E303", {"start": v(571.1, 1120.65) * mm, "mid": v(573.75, 1119.55) * mm, "end": v(574.85, 1116.9) * mm});
            skArc(sketch, "E304", {"start": v(574.85, 1116.9) * mm, "mid": v(573.75, 1114.25) * mm, "end": v(571.1, 1113.15) * mm});
            skArc(sketch, "E305", {"start": v(571.1, 1113.15) * mm, "mid": v(568.44, 1114.25) * mm, "end": v(567.35, 1116.9) * mm});
            skArc(sketch, "E306", {"start": v(567.35, 966.9) * mm, "mid": v(568.44, 969.55) * mm, "end": v(571.1, 970.65) * mm});
            skArc(sketch, "E307", {"start": v(571.1, 970.65) * mm, "mid": v(573.75, 969.55) * mm, "end": v(574.85, 966.9) * mm});
            skArc(sketch, "E308", {"start": v(574.85, 966.9) * mm, "mid": v(573.75, 964.25) * mm, "end": v(571.1, 963.15) * mm});
            skArc(sketch, "E309", {"start": v(571.1, 963.15) * mm, "mid": v(568.44, 964.25) * mm, "end": v(567.35, 966.9) * mm});
            skArc(sketch, "E310", {"start": v(567.35, 816.9) * mm, "mid": v(568.44, 819.55) * mm, "end": v(571.1, 820.65) * mm});
            skArc(sketch, "E311", {"start": v(571.1, 820.65) * mm, "mid": v(573.75, 819.55) * mm, "end": v(574.85, 816.9) * mm});
            skArc(sketch, "E312", {"start": v(574.85, 816.9) * mm, "mid": v(573.75, 814.25) * mm, "end": v(571.1, 813.15) * mm});
            skArc(sketch, "E313", {"start": v(571.1, 813.15) * mm, "mid": v(568.44, 814.25) * mm, "end": v(567.35, 816.9) * mm});
            skArc(sketch, "E314", {"start": v(567.35, 666.9) * mm, "mid": v(568.44, 669.55) * mm, "end": v(571.1, 670.65) * mm});
            skArc(sketch, "E315", {"start": v(571.1, 670.65) * mm, "mid": v(573.75, 669.55) * mm, "end": v(574.85, 666.9) * mm});
            skArc(sketch, "E316", {"start": v(574.85, 666.9) * mm, "mid": v(573.75, 664.25) * mm, "end": v(571.1, 663.15) * mm});
            skArc(sketch, "E317", {"start": v(571.1, 663.15) * mm, "mid": v(568.44, 664.25) * mm, "end": v(567.35, 666.9) * mm});
            skArc(sketch, "E318", {"start": v(567.35, 516.9) * mm, "mid": v(568.44, 519.55) * mm, "end": v(571.1, 520.65) * mm});
            skArc(sketch, "E319", {"start": v(571.1, 520.65) * mm, "mid": v(573.75, 519.55) * mm, "end": v(574.85, 516.9) * mm});
            skArc(sketch, "E320", {"start": v(574.85, 516.9) * mm, "mid": v(573.75, 514.25) * mm, "end": v(571.1, 513.15) * mm});
            skArc(sketch, "E321", {"start": v(571.1, 513.15) * mm, "mid": v(568.44, 514.25) * mm, "end": v(567.35, 516.9) * mm});
            skArc(sketch, "E322", {"start": v(567.35, 366.9) * mm, "mid": v(568.44, 369.55) * mm, "end": v(571.1, 370.65) * mm});
            skArc(sketch, "E323", {"start": v(571.1, 370.65) * mm, "mid": v(573.75, 369.55) * mm, "end": v(574.85, 366.9) * mm});
            skArc(sketch, "E324", {"start": v(574.85, 366.9) * mm, "mid": v(573.75, 364.25) * mm, "end": v(571.1, 363.15) * mm});
            skArc(sketch, "E325", {"start": v(571.1, 363.15) * mm, "mid": v(568.44, 364.25) * mm, "end": v(567.35, 366.9) * mm});
            skArc(sketch, "E326", {"start": v(567.35, 216.9) * mm, "mid": v(568.44, 219.55) * mm, "end": v(571.1, 220.65) * mm});
            skArc(sketch, "E327", {"start": v(571.1, 220.65) * mm, "mid": v(573.75, 219.55) * mm, "end": v(574.85, 216.9) * mm});
            skArc(sketch, "E328", {"start": v(574.85, 216.9) * mm, "mid": v(573.75, 214.25) * mm, "end": v(571.1, 213.15) * mm});
            skArc(sketch, "E329", {"start": v(571.1, 213.15) * mm, "mid": v(568.44, 214.25) * mm, "end": v(567.35, 216.9) * mm});
            skArc(sketch, "E330", {"start": v(567.35, 66.9) * mm, "mid": v(568.44, 69.55) * mm, "end": v(571.1, 70.65) * mm});
            skArc(sketch, "E331", {"start": v(571.1, 70.65) * mm, "mid": v(573.75, 69.55) * mm, "end": v(574.85, 66.9) * mm});
            skArc(sketch, "E332", {"start": v(574.85, 66.9) * mm, "mid": v(573.75, 64.25) * mm, "end": v(571.1, 63.15) * mm});
            skArc(sketch, "E333", {"start": v(571.1, 63.15) * mm, "mid": v(568.44, 64.25) * mm, "end": v(567.35, 66.9) * mm});
            skArc(sketch, "E334", {"start": v(567.35, -53.1) * mm, "mid": v(568.44, -50.45) * mm, "end": v(571.1, -49.35) * mm});
            skArc(sketch, "E335", {"start": v(571.1, -49.35) * mm, "mid": v(573.75, -50.45) * mm, "end": v(574.85, -53.1) * mm});
            skArc(sketch, "E336", {"start": v(574.85, -53.1) * mm, "mid": v(573.75, -55.75) * mm, "end": v(571.1, -56.85) * mm});
            skArc(sketch, "E337", {"start": v(571.1, -56.85) * mm, "mid": v(568.44, -55.75) * mm, "end": v(567.35, -53.1) * mm});
            skArc(sketch, "E338", {"start": v(567.35, -233.1) * mm, "mid": v(568.44, -230.45) * mm, "end": v(571.1, -229.35) * mm});
            skArc(sketch, "E339", {"start": v(571.1, -229.35) * mm, "mid": v(573.75, -230.45) * mm, "end": v(574.85, -233.1) * mm});
            skArc(sketch, "E340", {"start": v(574.85, -233.1) * mm, "mid": v(573.75, -235.75) * mm, "end": v(571.1, -236.85) * mm});
            skArc(sketch, "E341", {"start": v(571.1, -236.85) * mm, "mid": v(568.44, -235.75) * mm, "end": v(567.35, -233.1) * mm});
            skArc(sketch, "E342", {"start": v(567.35, -383.1) * mm, "mid": v(568.44, -380.45) * mm, "end": v(571.1, -379.35) * mm});
            skArc(sketch, "E343", {"start": v(571.1, -379.35) * mm, "mid": v(573.75, -380.45) * mm, "end": v(574.85, -383.1) * mm});
            skArc(sketch, "E344", {"start": v(574.85, -383.1) * mm, "mid": v(573.75, -385.75) * mm, "end": v(571.1, -386.85) * mm});
            skArc(sketch, "E345", {"start": v(571.1, -386.85) * mm, "mid": v(568.44, -385.75) * mm, "end": v(567.35, -383.1) * mm});
            skArc(sketch, "E346", {"start": v(567.35, -533.1) * mm, "mid": v(568.44, -530.45) * mm, "end": v(571.1, -529.35) * mm});
            skArc(sketch, "E347", {"start": v(571.1, -529.35) * mm, "mid": v(573.75, -530.45) * mm, "end": v(574.85, -533.1) * mm});
            skArc(sketch, "E348", {"start": v(574.85, -533.1) * mm, "mid": v(573.75, -535.75) * mm, "end": v(571.1, -536.85) * mm});
            skArc(sketch, "E349", {"start": v(571.1, -536.85) * mm, "mid": v(568.44, -535.75) * mm, "end": v(567.35, -533.1) * mm});
            skArc(sketch, "E350", {"start": v(567.35, -683.1) * mm, "mid": v(568.44, -680.45) * mm, "end": v(571.1, -679.35) * mm});
            skArc(sketch, "E351", {"start": v(571.1, -679.35) * mm, "mid": v(573.75, -680.45) * mm, "end": v(574.85, -683.1) * mm});
            skArc(sketch, "E352", {"start": v(574.85, -683.1) * mm, "mid": v(573.75, -685.75) * mm, "end": v(571.1, -686.85) * mm});
            skArc(sketch, "E353", {"start": v(571.1, -686.85) * mm, "mid": v(568.44, -685.75) * mm, "end": v(567.35, -683.1) * mm});
            skArc(sketch, "E354", {"start": v(567.35, -833.1) * mm, "mid": v(568.44, -830.45) * mm, "end": v(571.1, -829.35) * mm});
            skArc(sketch, "E355", {"start": v(571.1, -829.35) * mm, "mid": v(573.75, -830.45) * mm, "end": v(574.85, -833.1) * mm});
            skArc(sketch, "E356", {"start": v(574.85, -833.1) * mm, "mid": v(573.75, -835.75) * mm, "end": v(571.1, -836.85) * mm});
            skArc(sketch, "E357", {"start": v(571.1, -836.85) * mm, "mid": v(568.44, -835.75) * mm, "end": v(567.35, -833.1) * mm});
            skArc(sketch, "E358", {"start": v(567.35, -983.1) * mm, "mid": v(568.44, -980.45) * mm, "end": v(571.1, -979.35) * mm});
            skArc(sketch, "E359", {"start": v(571.1, -979.35) * mm, "mid": v(573.75, -980.45) * mm, "end": v(574.85, -983.1) * mm});
            skArc(sketch, "E360", {"start": v(574.85, -983.1) * mm, "mid": v(573.75, -985.75) * mm, "end": v(571.1, -986.85) * mm});
            skArc(sketch, "E361", {"start": v(571.1, -986.85) * mm, "mid": v(568.44, -985.75) * mm, "end": v(567.35, -983.1) * mm});
            skArc(sketch, "E362", {"start": v(567.35, -1133.1) * mm, "mid": v(568.44, -1130.45) * mm, "end": v(571.1, -1129.35) * mm});
            skArc(sketch, "E363", {"start": v(571.1, -1129.35) * mm, "mid": v(573.75, -1130.45) * mm, "end": v(574.85, -1133.1) * mm});
            skArc(sketch, "E364", {"start": v(574.85, -1133.1) * mm, "mid": v(573.75, -1135.75) * mm, "end": v(571.1, -1136.85) * mm});
            skArc(sketch, "E365", {"start": v(571.1, -1136.85) * mm, "mid": v(568.44, -1135.75) * mm, "end": v(567.35, -1133.1) * mm});
            skArc(sketch, "E366", {"start": v(567.35, -113.1) * mm, "mid": v(568.44, -110.45) * mm, "end": v(571.1, -109.35) * mm});
            skArc(sketch, "E367", {"start": v(571.1, -109.35) * mm, "mid": v(573.75, -110.45) * mm, "end": v(574.85, -113.1) * mm});
            skArc(sketch, "E368", {"start": v(574.85, -113.1) * mm, "mid": v(573.75, -115.75) * mm, "end": v(571.1, -116.85) * mm});
            skArc(sketch, "E369", {"start": v(571.1, -116.85) * mm, "mid": v(568.44, -115.75) * mm, "end": v(567.35, -113.1) * mm});
            skArc(sketch, "E370", {"start": v(2.97, -1064.68) * mm, "mid": v(0.32, -1065.77) * mm, "end": v(-0.78, -1068.43) * mm});
            skArc(sketch, "E371", {"start": v(-0.78, -1068.43) * mm, "mid": v(0.32, -1071.08) * mm, "end": v(2.97, -1072.18) * mm});
            skArc(sketch, "E372", {"start": v(2.97, -1072.18) * mm, "mid": v(5.62, -1071.08) * mm, "end": v(6.72, -1068.43) * mm});
            skArc(sketch, "E373", {"start": v(6.72, -1068.43) * mm, "mid": v(5.62, -1065.77) * mm, "end": v(2.97, -1064.68) * mm});
            skArc(sketch, "E374", {"start": v(-4.37, -602.57) * mm, "mid": v(-7.02, -603.67) * mm, "end": v(-8.12, -606.33) * mm});
            skArc(sketch, "E375", {"start": v(-8.12, -606.33) * mm, "mid": v(-7.02, -608.98) * mm, "end": v(-4.37, -610.08) * mm});
            skArc(sketch, "E376", {"start": v(-4.37, -610.08) * mm, "mid": v(-1.71, -608.98) * mm, "end": v(-0.62, -606.33) * mm});
            skArc(sketch, "E377", {"start": v(-0.62, -606.33) * mm, "mid": v(-1.71, -603.67) * mm, "end": v(-4.37, -602.57) * mm});
            skArc(sketch, "E378", {"start": v(-4.37, -206.49) * mm, "mid": v(-7.02, -207.59) * mm, "end": v(-8.12, -210.24) * mm});
            skArc(sketch, "E379", {"start": v(-8.12, -210.24) * mm, "mid": v(-7.02, -212.9) * mm, "end": v(-4.37, -213.99) * mm});
            skArc(sketch, "E380", {"start": v(-4.37, -213.99) * mm, "mid": v(-1.71, -212.9) * mm, "end": v(-0.62, -210.24) * mm});
            skArc(sketch, "E381", {"start": v(-0.62, -210.24) * mm, "mid": v(-1.71, -207.59) * mm, "end": v(-4.37, -206.49) * mm});
            skArc(sketch, "E382", {"start": v(-19.03, 284.95) * mm, "mid": v(-21.69, 283.85) * mm, "end": v(-22.78, 281.2) * mm});
            skArc(sketch, "E383", {"start": v(-22.78, 281.2) * mm, "mid": v(-21.69, 278.55) * mm, "end": v(-19.03, 277.45) * mm});
            skArc(sketch, "E384", {"start": v(-19.03, 277.45) * mm, "mid": v(-16.38, 278.55) * mm, "end": v(-15.28, 281.2) * mm});
            skArc(sketch, "E385", {"start": v(-15.28, 281.2) * mm, "mid": v(-16.38, 283.85) * mm, "end": v(-19.03, 284.95) * mm});
            skArc(sketch, "E386", {"start": v(2.97, 813.07) * mm, "mid": v(0.32, 811.97) * mm, "end": v(-0.78, 809.32) * mm});
            skArc(sketch, "E387", {"start": v(-0.78, 809.32) * mm, "mid": v(0.32, 806.66) * mm, "end": v(2.97, 805.57) * mm});
            skArc(sketch, "E388", {"start": v(2.97, 805.57) * mm, "mid": v(5.62, 806.66) * mm, "end": v(6.72, 809.32) * mm});
            skArc(sketch, "E389", {"start": v(6.72, 809.32) * mm, "mid": v(5.62, 811.97) * mm, "end": v(2.97, 813.07) * mm});
            skSolve(sketch);
        }
        {
            var Q0;
            {var subQ3=sQuery(id+"F0.wireOp",EDGE,"E4");Q0=makeQuery(id+"F0.imprint","IMPRINT",FACE,{"disambiguationData":[TD([[makeQuery(id+"F0.imprint","IMPRINT",EDGE,{"derivedFrom":subQ3}),1.0]])]});}
            extrude(context, id + "F1", {"entities" : qUnion([Q0]), "depth" : 18 * mm});
        }
    });
